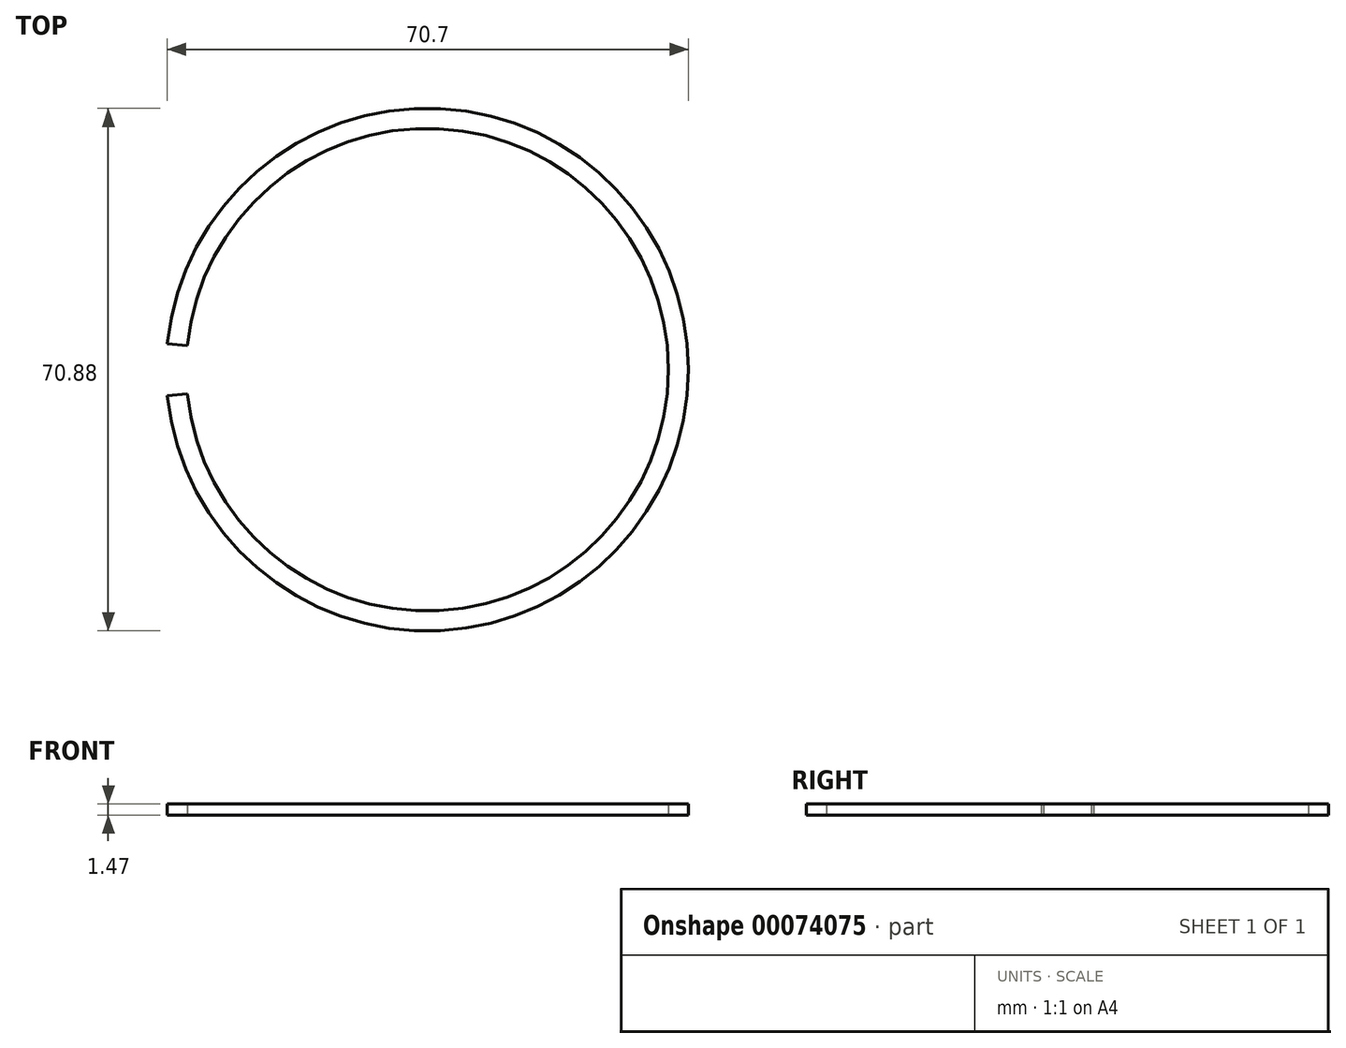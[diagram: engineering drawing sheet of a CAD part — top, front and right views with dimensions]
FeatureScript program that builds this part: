
annotation { "Feature Type Name" : "Feature", "Feature Type Description" : "" }
export const myFeature = defineFeature(function(context is Context, id is Id, definition is map)
    precondition{}
    {
        {
            var Q0;
            Q0=qCreatedBy(makeId("Top.planeOp"),FACE);
            var sketch = newSketch(context, id + "F0", { "sketchPlane" : qUnion([Q0])});
            skArc(sketch, "E0", {"start": v(-35.26, -3.54) * mm, "mid": v(35.44, 0) * mm, "end": v(-35.26, 3.54) * mm});
            skArc(sketch, "E1", {"start": v(-32.56, -3.27) * mm, "mid": v(32.72, 0) * mm, "end": v(-32.56, 3.27) * mm});
            skLineSegment(sketch, "E2", {"start": v(0, 0) * mm, "end": v(-35.26, -3.54) * mm});
            skLineSegment(sketch, "E3", {"start": v(-35.26, -3.54) * mm, "end": v(-32.56, -3.27) * mm});
            skLineSegment(sketch, "E4", {"start": v(-35.26, 3.54) * mm, "end": v(-32.56, 3.27) * mm});
            skSolve(sketch);
        }
        {
            var Q0;
            Q0=makeQuery(id+"F0.imprint","IMPRINT",FACE,{"disambiguationData":[TD([[makeQuery(id+"F0.imprint","IMPRINT",EDGE,{"derivedFrom":sQuery(id+"F0.wireOp",EDGE,"E0")}),1.0]])]});
            extrude(context, id + "F1", {"entities" : qUnion([Q0]), "depth" : 1.47 * mm});
        }
    });
